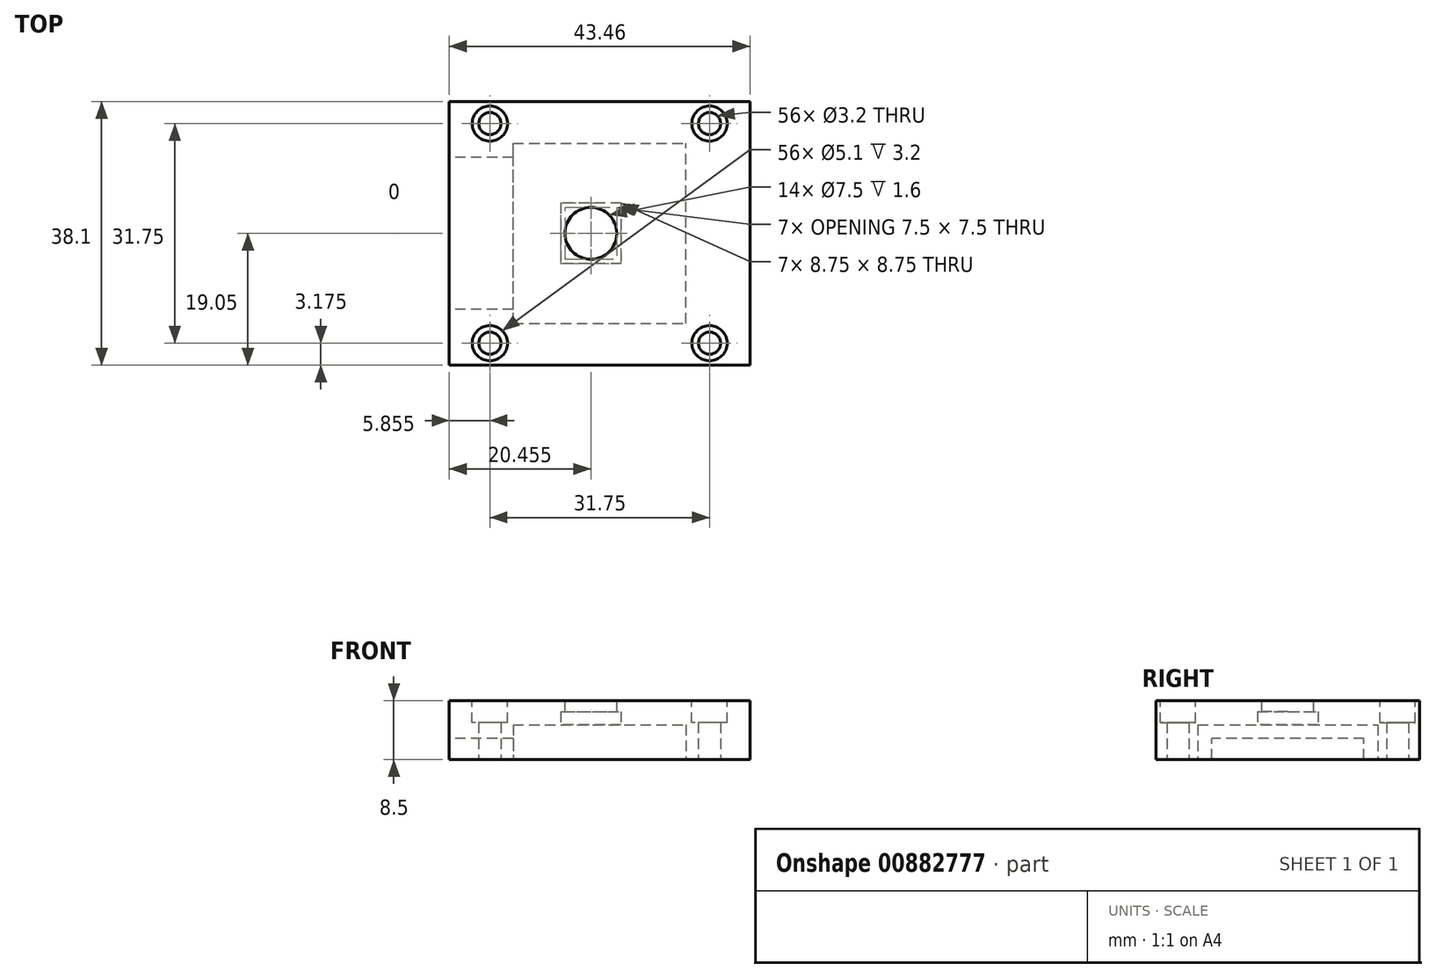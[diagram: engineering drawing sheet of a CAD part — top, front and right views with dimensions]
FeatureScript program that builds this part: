
annotation { "Feature Type Name" : "Feature", "Feature Type Description" : "" }
export const myFeature = defineFeature(function(context is Context, id is Id, definition is map)
    precondition{}
    {
        {
            var Q0;
            Q0=qCreatedBy(makeId("Top.planeOp"),FACE);
            var sketch = newSketch(context, id + "F0", { "sketchPlane" : qUnion([Q0])});
            skLineSegment(sketch, "E0.bottom", {"start": v(21.73, -19.05) * mm, "end": v(-21.73, -19.05) * mm});
            skLineSegment(sketch, "E0.top", {"start": v(21.73, 19.05) * mm, "end": v(-21.73, 19.05) * mm});
            skLineSegment(sketch, "E0.left", {"start": v(21.73, -19.05) * mm, "end": v(21.73, 19.05) * mm});
            skLineSegment(sketch, "E0.right", {"start": v(-21.73, -19.05) * mm, "end": v(-21.73, 19.05) * mm});
            skPoint(sketch, "E0.middle", {"position": v(0, 0) * mm});
            skCircle(sketch, "E1", {"center": v(-15.87, 15.87) * mm, "radius": 1.6 * mm});
            skCircle(sketch, "E2", {"center": v(15.87, 15.87) * mm, "radius": 1.6 * mm});
            skCircle(sketch, "E3", {"center": v(15.87, -15.87) * mm, "radius": 1.6 * mm});
            skCircle(sketch, "E4", {"center": v(-15.87, -15.87) * mm, "radius": 1.6 * mm});
            skSolve(sketch);
        }
        {
            var Q0;
            Q0 = qSketchRegion(id + "F0", true);
            extrude(context, id + "F1", {"entities" : qUnion([Q0]), "depth" : 8.5 * mm, "offsetDistance" : 25.4 * mm});
        }
        {
            var Q0;
            Q0=makeQuery(id+"F1.opExtrude","CAP_FACE",FACE,{"disambiguationData":[OSD([sQuery(id+"F0.wireOp",EDGE,"E0.bottom"),sQuery(id+"F0.wireOp",EDGE,"E0.top"),sQuery(id+"F0.wireOp",EDGE,"E0.left"),sQuery(id+"F0.wireOp",EDGE,"E0.right"),sQuery(id+"F0.wireOp",EDGE,"E1"),sQuery(id+"F0.wireOp",EDGE,"E2"),sQuery(id+"F0.wireOp",EDGE,"E3"),sQuery(id+"F0.wireOp",EDGE,"E4")])],"isStart":false});
            var sketch = newSketch(context, id + "F2", { "sketchPlane" : qUnion([Q0])});
            skCircle(sketch, "E5", {"center": v(-15.87, 15.87) * mm, "radius": 2.55 * mm});
            skCircle(sketch, "E6", {"center": v(-15.87, -15.87) * mm, "radius": 2.55 * mm});
            skCircle(sketch, "E7.MirrorC", {"center": v(15.87, 15.87) * mm, "radius": 2.55 * mm});
            skCircle(sketch, "E8.MirrorC", {"center": v(15.87, -15.87) * mm, "radius": 2.55 * mm});
            skSolve(sketch);
        }
        {
            var Q0;
            Q0 = qSketchRegion(id + "F2", true);
            extrude(context, id + "F3", {"entities" : qUnion([Q0]), "operationType" : NewBodyOperationType.REMOVE, "oppositeDirection" : true, "depth" : 3.2 * mm, "offsetDistance" : 25.4 * mm});
        }
        {
            var Q0;
            Q0=makeQuery(id+"F1.opExtrude","CAP_FACE",FACE,{"disambiguationData":[OSD([sQuery(id+"F0.wireOp",EDGE,"E0.bottom"),sQuery(id+"F0.wireOp",EDGE,"E0.top"),sQuery(id+"F0.wireOp",EDGE,"E0.left"),sQuery(id+"F0.wireOp",EDGE,"E0.right"),sQuery(id+"F0.wireOp",EDGE,"E1"),sQuery(id+"F0.wireOp",EDGE,"E2"),sQuery(id+"F0.wireOp",EDGE,"E3"),sQuery(id+"F0.wireOp",EDGE,"E4")])],"isStart":false});
            var sketch = newSketch(context, id + "F4", { "sketchPlane" : qUnion([Q0])});
            skCircle(sketch, "E9", {"center": v(-1.27, 0) * mm, "radius": 3.75 * mm});
            skSolve(sketch);
        }
        {
            var Q0;
            Q0 = qSketchRegion(id + "F4", true);
            extrude(context, id + "F5", {"entities" : qUnion([Q0]), "operationType" : NewBodyOperationType.REMOVE, "endBound" : BoundingType.UP_TO_NEXT, "oppositeDirection" : true, "depth" : 25.4 * mm, "offsetDistance" : 25.4 * mm});
        }
        {
            var Q0;
            Q0=makeQuery(id+"F1.opExtrude","CAP_FACE",FACE,{"disambiguationData":[OSD([sQuery(id+"F0.wireOp",EDGE,"E0.bottom"),sQuery(id+"F0.wireOp",EDGE,"E0.top"),sQuery(id+"F0.wireOp",EDGE,"E0.left"),sQuery(id+"F0.wireOp",EDGE,"E0.right"),sQuery(id+"F0.wireOp",EDGE,"E1"),sQuery(id+"F0.wireOp",EDGE,"E2"),sQuery(id+"F0.wireOp",EDGE,"E3"),sQuery(id+"F0.wireOp",EDGE,"E4")])],"isStart":true});
            var sketch = newSketch(context, id + "F6", { "sketchPlane" : qUnion([Q0])});
            skLineSegment(sketch, "E10.bottom", {"start": v(-5.65, 4.37) * mm, "end": v(3.1, 4.38) * mm});
            skLineSegment(sketch, "E10.top", {"start": v(-5.65, -4.38) * mm, "end": v(3.1, -4.38) * mm});
            skLineSegment(sketch, "E10.left", {"start": v(-5.65, 4.37) * mm, "end": v(-5.65, -4.38) * mm});
            skLineSegment(sketch, "E10.right", {"start": v(3.1, 4.38) * mm, "end": v(3.1, -4.37) * mm});
            skPoint(sketch, "E10.middle", {"position": v(-1.27, 0) * mm});
            skSolve(sketch);
        }
        {
            var Q0;
            Q0 = qSketchRegion(id + "F6", true);
            extrude(context, id + "F7", {"entities" : qUnion([Q0]), "operationType" : NewBodyOperationType.REMOVE, "oppositeDirection" : true, "depth" : 6.9 * mm, "offsetDistance" : 25.4 * mm});
        }
        {
            var Q0;
            Q0=makeQuery(id+"F1.opExtrude","CAP_FACE",FACE,{"disambiguationData":[OSD([sQuery(id+"F0.wireOp",EDGE,"E0.bottom"),sQuery(id+"F0.wireOp",EDGE,"E0.top"),sQuery(id+"F0.wireOp",EDGE,"E0.left"),sQuery(id+"F0.wireOp",EDGE,"E0.right"),sQuery(id+"F0.wireOp",EDGE,"E1"),sQuery(id+"F0.wireOp",EDGE,"E2"),sQuery(id+"F0.wireOp",EDGE,"E3"),sQuery(id+"F0.wireOp",EDGE,"E4")])],"isStart":true});
            var sketch = newSketch(context, id + "F8", { "sketchPlane" : qUnion([Q0])});
            skLineSegment(sketch, "E11.bottom", {"start": v(-12.5, 13) * mm, "end": v(12.5, 13) * mm});
            skLineSegment(sketch, "E11.top", {"start": v(-12.5, -13) * mm, "end": v(12.5, -13) * mm});
            skLineSegment(sketch, "E11.left", {"start": v(-12.5, 13) * mm, "end": v(-12.5, -13) * mm});
            skLineSegment(sketch, "E11.right", {"start": v(12.5, 13) * mm, "end": v(12.5, -13) * mm});
            skPoint(sketch, "E11.middle", {"position": v(0, 0) * mm});
            skSolve(sketch);
        }
        {
            var Q0;
            Q0 = qSketchRegion(id + "F8", true);
            extrude(context, id + "F9", {"entities" : qUnion([Q0]), "operationType" : NewBodyOperationType.REMOVE, "oppositeDirection" : true, "depth" : 8.5 * mm - 2 * mm - 1.5 * mm, "offsetDistance" : 25.4 * mm});
        }
        {
            var Q0;
            Q0=makeQuery(id+"F1.opExtrude","SWEPT_FACE",FACE,{"disambiguationData":[OSD([sQuery(id+"F0.wireOp",EDGE,"E0.right")])]});
            var sketch = newSketch(context, id + "F10", { "sketchPlane" : qUnion([Q0])});
            skLineSegment(sketch, "E12.bottom", {"start": v(-11, 0) * mm, "end": v(11, 0) * mm});
            skLineSegment(sketch, "E12.top", {"start": v(-11, 3) * mm, "end": v(11, 3) * mm});
            skLineSegment(sketch, "E12.left", {"start": v(-11, 0) * mm, "end": v(-11, 3) * mm});
            skLineSegment(sketch, "E12.right", {"start": v(11, 0) * mm, "end": v(11, 3) * mm});
            skSolve(sketch);
        }
        {
            var Q0;
            Q0 = qSketchRegion(id + "F10", true);
            extrude(context, id + "F11", {"entities" : qUnion([Q0]), "operationType" : NewBodyOperationType.REMOVE, "endBound" : BoundingType.UP_TO_NEXT, "oppositeDirection" : true, "depth" : 25.4 * mm, "offsetDistance" : 25.4 * mm});
        }
    });
